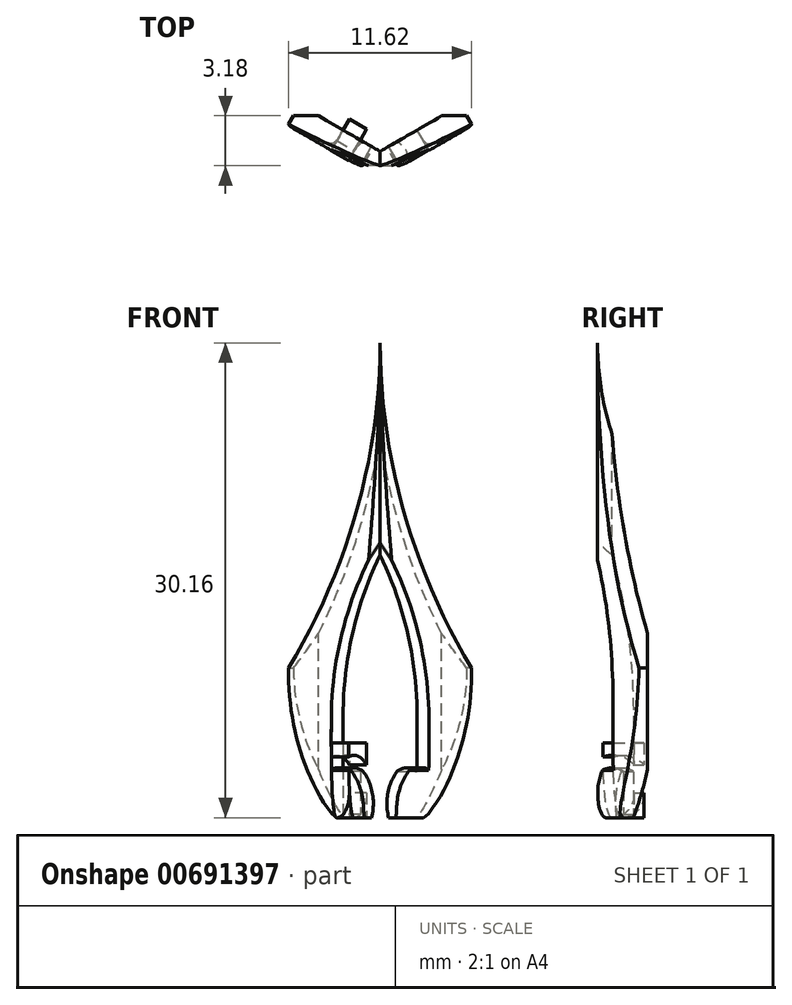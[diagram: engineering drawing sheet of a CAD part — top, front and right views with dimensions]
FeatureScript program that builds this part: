
annotation { "Feature Type Name" : "Feature", "Feature Type Description" : "" }
export const myFeature = defineFeature(function(context is Context, id is Id, definition is map)
    precondition{}
    {
        {
            var Q0;
            Q0=qCreatedBy(makeId("Top.planeOp"),FACE);
            var sketch = newSketch(context, id + "F0", { "sketchPlane" : qUnion([Q0])});
            skCircle(sketch, "E0", {"center": v(0, 0) * mm, "radius": 6.35 * mm});
            skCircle(sketch, "E1.cCircle", {"center": v(0, 0) * mm, "radius": 6.35 * mm, "construction": true});
            skLineSegment(sketch, "E1.0", {"start": v(0, 6.35) * mm, "end": v(5.5, -3.17) * mm});
            skLineSegment(sketch, "E1.1", {"start": v(5.5, -3.17) * mm, "end": v(-5.5, -3.18) * mm});
            skLineSegment(sketch, "E1.2", {"start": v(-5.5, -3.18) * mm, "end": v(0, 6.35) * mm});
            skLineSegment(sketch, "E2", {"start": v(5.5, -3.18) * mm, "end": v(-2.75, 1.59) * mm});
            skLineSegment(sketch, "E3", {"start": v(-5.5, -3.18) * mm, "end": v(2.75, 1.59) * mm});
            skLineSegment(sketch, "E4", {"start": v(0, -3.18) * mm, "end": v(0, 6.35) * mm});
            skLineSegment(sketch, "E5.0", {"start": v(-3.3, -1.9) * mm, "end": v(0, 3.8) * mm});
            skLineSegment(sketch, "E5.1", {"start": v(3.3, -1.9) * mm, "end": v(-3.3, -1.9) * mm});
            skLineSegment(sketch, "E5.2", {"start": v(0, 3.8) * mm, "end": v(3.3, -1.9) * mm});
            skPoint(sketch, "E6", {"position": v(-1.65, 0.95) * mm});
            skPoint(sketch, "E6.positionSnap0", {"position": v(-1.65, 0.95) * mm});
            skPoint(sketch, "E7", {"position": v(1.65, 0.95) * mm});
            skLineSegment(sketch, "E8", {"start": v(-2.75, 1.59) * mm, "end": v(-5.5, 3.17) * mm});
            skLineSegment(sketch, "E9", {"start": v(2.75, 1.59) * mm, "end": v(5.5, 3.18) * mm});
            skSolve(sketch);
        }
        {
            var Q0;
            Q0=qCreatedBy(makeId("Front.planeOp"),FACE);
            var sketch = newSketch(context, id + "F1", { "sketchPlane" : qUnion([Q0])});
            skLineSegment(sketch, "E10", {"start": v(0, 0) * mm, "end": v(0, 25.4) * mm});
            skSolve(sketch);
        }
        {
            var Q0;
            Q0=sQuery(id+"F0.wireOp",VERTEX,"E1.2.end");
            var Q1;
            Q1=sQuery(id+"F1.wireOp",VERTEX,"E10.end");
            var Q2;
            Q2=sQuery(id+"F0.wireOp",VERTEX,"E4.start");
            cPlane(context, id + "F2", {"entities" : qUnion([Q0, Q1, Q2]), "cplaneType" : CPlaneType.THREE_POINT, "offset" : 25.4 * mm, "width" : 152.4 * mm, "height" : 152.4 * mm});
        }
        {
            var Q0;
            Q0=sQuery(id+"F0.wireOp",VERTEX,"E2.end");
            var Q1;
            Q1=sQuery(id+"F1.wireOp",VERTEX,"E10.end");
            var Q2;
            Q2=sQuery(id+"F0.wireOp",VERTEX,"E1.0.end");
            cPlane(context, id + "F3", {"entities" : qUnion([Q0, Q1, Q2]), "cplaneType" : CPlaneType.THREE_POINT, "offset" : 25.4 * mm, "width" : 152.4 * mm, "height" : 152.4 * mm});
        }
        {
            var Q0;
            Q0=qCreatedBy(id+"F3.planeOp",FACE);
            var sketch = newSketch(context, id + "F4", { "sketchPlane" : qUnion([Q0])});
            skLineSegment(sketch, "E11", {"start": v(-6.35, 0) * mm, "end": v(-6.35, 4.76) * mm});
            skLineSegment(sketch, "E12", {"start": v(0, 0) * mm, "end": v(0, 25.4) * mm});
            skLineSegment(sketch, "E13", {"start": v(-3.17, 0) * mm, "end": v(-3.17, -6.35) * mm});
            skLineSegment(sketch, "E14", {"start": v(-1.9, 0) * mm, "end": v(-1.9, -3.18) * mm});
            skPoint(sketch, "E15", {"position": v(0, 12.7) * mm});
            skLineSegment(sketch, "E16", {"start": v(-3.17, 0) * mm, "end": v(-3.17, 1.59) * mm});
            skPoint(sketch, "E17", {"position": v(-3.17, 0) * mm});
            skPoint(sketch, "E18", {"position": v(-1.9, -1.59) * mm});
            skLineSegment(sketch, "E19", {"start": v(-1.9, -1.59) * mm, "end": v(-1.9, -2.38) * mm});
            skSolve(sketch);
        }
        {
            var Q0;
            Q0=qCreatedBy(id+"F3.planeOp",FACE);
            var sketch = newSketch(context, id + "F5", { "sketchPlane" : qUnion([Q0])});
            skLineSegment(sketch, "E20", {"start": v(0, 25.4) * mm, "end": v(0, 12.7) * mm});
            skArc(sketch, "E21", {"start": v(-6.35, 4.76) * mm, "mid": v(-1.62, 14.6) * mm, "end": v(0, 25.4) * mm});
            skArc(sketch, "E22", {"start": v(0, 12.7) * mm, "mid": v(-2.37, 7.37) * mm, "end": v(-3.17, 1.59) * mm});
            skPoint(sketch, "E23.left.start.orphan", {"position": v(-1.9, -1.59) * mm});
            skLineSegment(sketch, "E24", {"start": v(-3.17, 1.59) * mm, "end": v(-3.17, -1.59) * mm});
            skPoint(sketch, "E25.1.internal.orphan", {"position": v(-3.17, -4.76) * mm});
            skLineSegment(sketch, "E26", {"start": v(-3.17, -1.59) * mm, "end": v(-1.9, -1.59) * mm});
            skArc(sketch, "E27", {"start": v(-6.35, 4.76) * mm, "mid": v(-5.54, -0.26) * mm, "end": v(-3.17, -4.76) * mm});
            skLineSegment(sketch, "E28", {"start": v(-3.17, -4.76) * mm, "end": v(-1.9, -4.76) * mm});
            skArc(sketch, "E29", {"start": v(-1.9, -6.12) * mm, "mid": v(-0.96, -3.85) * mm, "end": v(-1.9, -1.59) * mm});
            skLineSegment(sketch, "E30", {"start": v(-1.9, -4.76) * mm, "end": v(-1.9, -6.12) * mm});
            skSolve(sketch);
        }
        {
            var Q0;
            Q0=sQuery(id+"F0.wireOp",VERTEX,"E3.start");
            var Q1;
            Q1=sQuery(id+"F0.wireOp",VERTEX,"E3.end");
            var Q2;
            Q2=sQuery(id+"F1.wireOp",VERTEX,"E10.end");
            cPlane(context, id + "F6", {"entities" : qUnion([Q0, Q1, Q2]), "cplaneType" : CPlaneType.THREE_POINT, "offset" : 25.4 * mm, "width" : 152.4 * mm, "height" : 152.4 * mm});
        }
        {
            var Q0;
            Q0=qCreatedBy(id+"F6.planeOp",FACE);
            var sketch = newSketch(context, id + "F7", { "sketchPlane" : qUnion([Q0])});
            skLineSegment(sketch, "E31", {"start": v(-6.35, 0) * mm, "end": v(-6.35, 3.18) * mm});
            skLineSegment(sketch, "E32", {"start": v(-1.9, 0) * mm, "end": v(-1.9, -3.18) * mm});
            skLineSegment(sketch, "E33", {"start": v(-3.17, 0) * mm, "end": v(-3.17, -6.35) * mm});
            skLineSegment(sketch, "E34", {"start": v(-3.17, 0) * mm, "end": v(-3.17, 1.59) * mm});
            skSolve(sketch);
        }
        {
            var Q0;
            Q0=qCreatedBy(id+"F6.planeOp",FACE);
            var sketch = newSketch(context, id + "F8", { "sketchPlane" : qUnion([Q0])});
            skLineSegment(sketch, "E35", {"start": v(0, 25.4) * mm, "end": v(0, 12.7) * mm});
            skArc(sketch, "E36", {"start": v(-6.35, 3.18) * mm, "mid": v(-1.62, 13.84) * mm, "end": v(0, 25.4) * mm});
            skLineSegment(sketch, "E37", {"start": v(-3.17, -6.35) * mm, "end": v(-3.17, 1.59) * mm});
            skArc(sketch, "E38", {"start": v(0, 12.7) * mm, "mid": v(-2.37, 7.37) * mm, "end": v(-3.18, 1.59) * mm});
            skArc(sketch, "E39", {"start": v(-6.35, 3.17) * mm, "mid": v(-5.54, -1.85) * mm, "end": v(-3.18, -6.35) * mm});
            skSolve(sketch);
        }
        {
            var Q0;
            Q0=qCreatedBy(makeId("Top.planeOp"),FACE);
            var sketch = newSketch(context, id + "F9", { "sketchPlane" : qUnion([Q0])});
            skLineSegment(sketch, "E40.0", {"start": v(0, 6.35) * mm, "end": v(5.5, -3.17) * mm});
            skLineSegment(sketch, "E40.1", {"start": v(5.5, -3.17) * mm, "end": v(-5.5, -3.18) * mm});
            skLineSegment(sketch, "E40.2", {"start": v(-5.5, -3.18) * mm, "end": v(0, 6.35) * mm});
            skLineSegment(sketch, "E41.0", {"start": v(-3.3, -1.9) * mm, "end": v(0, 3.8) * mm});
            skLineSegment(sketch, "E41.1", {"start": v(3.3, -1.9) * mm, "end": v(-3.3, -1.9) * mm});
            skLineSegment(sketch, "E41.2", {"start": v(0, 3.8) * mm, "end": v(3.3, -1.9) * mm});
            skPoint(sketch, "E42", {"position": v(-1.65, 0.95) * mm});
            skPoint(sketch, "E42.positionSnap0", {"position": v(-1.65, 0.95) * mm});
            skPoint(sketch, "E43", {"position": v(1.65, 0.95) * mm});
            skPoint(sketch, "E44.center.orphan", {"position": v(0, 0) * mm});
            skPoint(sketch, "E45.start.orphan", {"position": v(0, -3.17) * mm});
            skPoint(sketch, "E46.start.orphan", {"position": v(2.75, 1.59) * mm});
            skPoint(sketch, "E47.start.orphan", {"position": v(-2.75, 1.59) * mm});
            skSolve(sketch);
        }
        {
            var Q0;
            Q0=makeQuery(id+"F9.imprint","IMPRINT",FACE,{"disambiguationData":[TD([[makeQuery(id+"F9.imprint","IMPRINT",EDGE,{"derivedFrom":sQuery(id+"F9.wireOp",EDGE,"E40.0")}),-1.0]])]});
            extrude(context, id + "F10", {"entities" : qUnion([Q0]), "oppositeDirection" : true, "depth" : 152.4 * mm, "offsetDistance" : 25.4 * mm});
        }
        {
            var Q0;
            Q0=makeQuery(id+"F10.opExtrude","SWEPT_FACE",FACE,{"disambiguationData":[OSD([sQuery(id+"F9.wireOp",EDGE,"E40.2")])]});
            var Q1;
            Q1=makeQuery(id+"F10.opExtrude","CAP_VERTEX",VERTEX,{"disambiguationData":[OSD([sQuery(id+"F9.wireOp",EDGE,"E40.0"),sQuery(id+"F9.wireOp",EDGE,"E40.2")])],"isStart":true});
            cPlane(context, id + "F11", {"entities" : qUnion([Q0, Q1]), "cplaneType" : CPlaneType.PLANE_POINT, "offset" : 25.4 * mm, "width" : 152.4 * mm, "height" : 152.4 * mm});
        }
        {
            var Q0;
            Q0=qCreatedBy(id+"F11.planeOp",FACE);
            var sketch = newSketch(context, id + "F12", { "sketchPlane" : qUnion([Q0])});
            skCircle(sketch, "E48", {"center": v(0, -3.18) * mm, "radius": 1.59 * mm});
            skCircle(sketch, "E49", {"center": v(0, -3.18) * mm, "radius": 2.38 * mm});
            skLineSegment(sketch, "E50", {"start": v(-2.38, -3.18) * mm, "end": v(2.38, -3.18) * mm});
            skSolve(sketch);
        }
        {
            var Q0;
            Q0=makeQuery(id+"F12.imprint","IMPRINT",FACE,{"disambiguationData":[TD([[makeQuery(id+"F12.imprint","IMPRINT",EDGE,{"derivedFrom":sQuery(id+"F12.wireOp",EDGE,"E48")}),1.0]])]});
            extrude(context, id + "F13", {"entities" : qUnion([Q0]), "operationType" : NewBodyOperationType.REMOVE, "oppositeDirection" : true, "depth" : 1.27 * mm, "offsetDistance" : 25.4 * mm});
        }
        {
            var Q0;
            Q0=makeQuery(id+"F5.imprint","IMPRINT",FACE,{"disambiguationData":[TD([[makeQuery(id+"F5.imprint","IMPRINT",EDGE,{"derivedFrom":sQuery(id+"F5.wireOp",EDGE,"E20")}),-1.0]])]});
            extrude(context, id + "F14", {"entities" : qUnion([Q0]), "depth" : 1.59 * mm, "offsetDistance" : 25.4 * mm, "hasSecondDirection" : true, "secondDirectionOppositeDirection" : true, "secondDirectionDepth" : 0.8 * mm});
        }
        {
            var Q0;
            Q0=qCreatedBy(id+"F11.planeOp",FACE);
            var sketch = newSketch(context, id + "F15", { "sketchPlane" : qUnion([Q0])});
            skFitSpline(sketch, "E51", {"points": [v(0, -4.76) * mm, v(0, 25.4) * mm], "startDerivative": vector(4.76, 0) * mm, "endDerivative": vector(0, 38.1) * mm});
            skLineSegment(sketch, "E52.bottom", {"start": v(0, 25.4) * mm, "end": v(-1.59, 25.4) * mm});
            skLineSegment(sketch, "E52.top", {"start": v(0, -4.76) * mm, "end": v(-1.59, -4.76) * mm});
            skLineSegment(sketch, "E52.right", {"start": v(-1.59, 25.4) * mm, "end": v(-1.59, -4.76) * mm});
            skSolve(sketch);
        }
        {
            var Q0;
            Q0=makeQuery(id+"F15.imprint","IMPRINT",FACE,{"disambiguationData":[TD([[makeQuery(id+"F15.imprint","IMPRINT",EDGE,{"derivedFrom":sQuery(id+"F15.wireOp",EDGE,"E51")}),1.0]])]});
            extrude(context, id + "F16", {"entities" : qUnion([Q0]), "operationType" : NewBodyOperationType.INTERSECT, "depth" : 6.35 * mm, "offsetDistance" : 25.4 * mm, "hasSecondDirection" : true, "secondDirectionOppositeDirection" : true, "secondDirectionDepth" : 6.35 * mm});
        }
        {
            var Q0;
            {var subQ0=sQuery(id+"F12.wireOp",EDGE,"E50");var subQ1=sQuery(id+"F12.wireOp",EDGE,"E48");var subQ2=makeQuery(id+"F12.imprint","INTERSECT",VERTEX,{"disambiguationData":[OD(0.0)],"derivedFrom":[subQ1,subQ0]});Q0=makeQuery(id+"F12.imprint","IMPRINT",FACE,{"disambiguationData":[TD([[makeQuery(id+"F12.imprint","IMPRINT",EDGE,{"disambiguationData":[TD([[subQ2,1.0]])],"derivedFrom":subQ1}),-1.0]])]});}
            extrude(context, id + "F17", {"entities" : qUnion([Q0]), "operationType" : NewBodyOperationType.REMOVE, "oppositeDirection" : true, "depth" : 2.54 * mm, "offsetDistance" : 25.4 * mm});
        }
        {
            var Q0;
            Q0=qCreatedBy(makeId("Front.planeOp"),FACE);
            var sketch = newSketch(context, id + "F18", { "sketchPlane" : qUnion([Q0])});
            skLineSegment(sketch, "E53.bottom", {"start": v(0, -6.35) * mm, "end": v(-6.35, -6.35) * mm});
            skLineSegment(sketch, "E53.top", {"start": v(0, 25.4) * mm, "end": v(-6.35, 25.4) * mm});
            skLineSegment(sketch, "E53.left", {"start": v(0, -6.35) * mm, "end": v(0, 25.4) * mm});
            skLineSegment(sketch, "E53.right", {"start": v(-6.35, -6.35) * mm, "end": v(-6.35, 25.4) * mm});
            skSolve(sketch);
        }
        {
            var Q0;
            Q0=makeQuery(id+"F18.imprint","IMPRINT",FACE,{"disambiguationData":[TD([[makeQuery(id+"F18.imprint","IMPRINT",EDGE,{"derivedFrom":sQuery(id+"F18.wireOp",EDGE,"E53.bottom")}),-1.0]])]});
            extrude(context, id + "F19", {"entities" : qUnion([Q0]), "operationType" : NewBodyOperationType.INTERSECT, "oppositeDirection" : true, "depth" : 3.17 * mm, "offsetDistance" : 25.4 * mm});
        }
        {
            var Q0;
            Q0=makeQuery(id+"F14.opExtrude","SWEPT_BODY",BODY,{"disambiguationData":[OSD([sQuery(id+"F5.wireOp",EDGE,"E20"),sQuery(id+"F5.wireOp",EDGE,"E21"),sQuery(id+"F5.wireOp",EDGE,"E22"),sQuery(id+"F5.wireOp",EDGE,"E24"),sQuery(id+"F5.wireOp",EDGE,"E26"),sQuery(id+"F5.wireOp",EDGE,"E27"),sQuery(id+"F5.wireOp",EDGE,"E28"),sQuery(id+"F5.wireOp",EDGE,"E29"),sQuery(id+"F5.wireOp",EDGE,"E30")])]});
            var Q1;
            Q1=qCreatedBy(id+"F2.planeOp",FACE);
            mirror(context, id + "F20", {"entities" : qUnion([Q0]), "mirrorPlane" : qUnion([Q1])});
        }
    });
